# Revit family: PAYE  S610 3M  1T 60W
name_source: partatom
category: Lighting Fixtures
revit_build: Autodesk Revit 2017 (Build: 20160225_1515(x64)
units: mm (PartAtom-declared; Revit-internal decimal feet)

## family parameters
Cut with Voids When Loaded = No
Host = Face
Light Source = No
Part Type = Normal
Room Calculation Point = No
Round Connector Dimension = Use Diameter
Shared = No

## types (2) — shared parameters
Body Material = IRON
Default Elevation = 122 cm
Height = 300 cm
IP = IP66
Lamp = LED
Manufacturer = SHOA
Model = PAYE  S610 3M  1T 60W
Protection Class = Class I
Type medule = SMD
Voltage/Frequency = 230v/50hz
Wattage. = 60 W
Width = 89 cm
body color = Black Body
color rendering index(CRI) = >70
color temperature = 3000K-6500K
consumption current = 0 A
website = www.shoaco.com

## per-type parameters (varying)
| type | 3000K | 6500K |
| PAYE  S610 3M  1T 60W(Black color-6500K-LED) | No | Yes |
| PAYE  S610 3M  1T 60W(Black color-3000K-LED) | Yes | No |

## geometry (parser evidence)
native form markers: Sweep x4
no freeform markers — native parametric forms only
